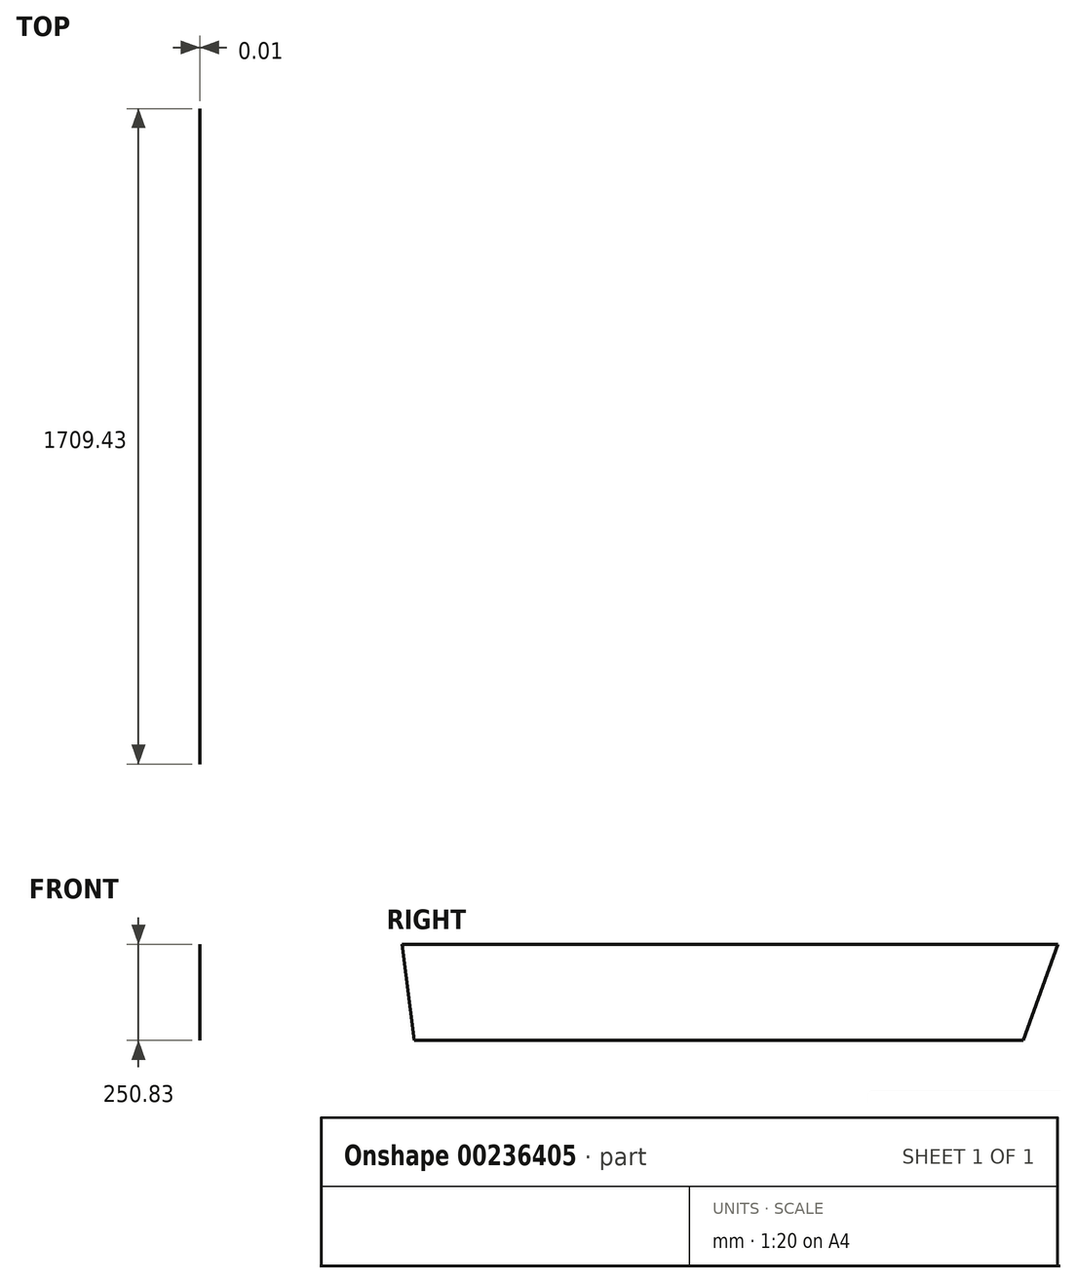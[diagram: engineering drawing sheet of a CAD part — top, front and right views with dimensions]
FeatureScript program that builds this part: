
annotation { "Feature Type Name" : "Feature", "Feature Type Description" : "" }
export const myFeature = defineFeature(function(context is Context, id is Id, definition is map)
    precondition{}
    {
        {
            var Q0;
            Q0=qCreatedBy(makeId("Right.planeOp"),FACE);
            var sketch = newSketch(context, id + "F0", { "sketchPlane" : qUnion([Q0])});
            skLineSegment(sketch, "E0", {"start": v(-808.75, -127) * mm, "end": v(-839.86, 123.82) * mm});
            skLineSegment(sketch, "E1", {"start": v(-839.86, 123.82) * mm, "end": v(869.57, 123.82) * mm});
            skLineSegment(sketch, "E2", {"start": v(869.57, 123.82) * mm, "end": v(778.27, -127) * mm});
            skLineSegment(sketch, "E3", {"start": v(778.27, -127) * mm, "end": v(-808.75, -127) * mm});
            skSolve(sketch);
        }
        {
            var Q0;
            Q0 = qSketchRegion(id + "F0", true);
            extrude(context, id + "F1", {"entities" : qUnion([Q0]), "depth" : 3 / 406.4 * mm});
        }
    });
